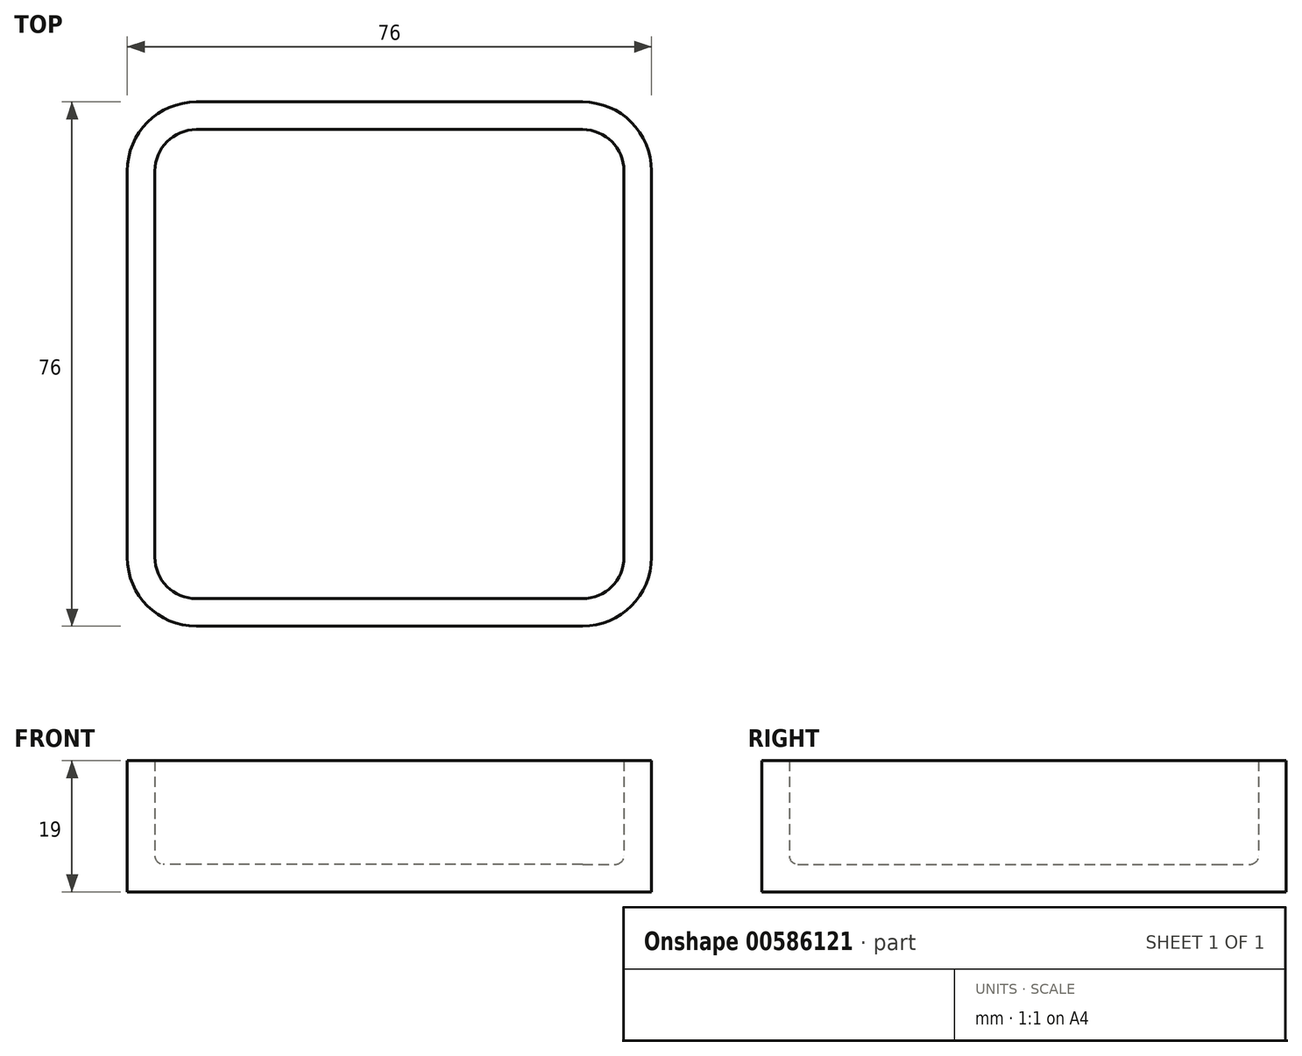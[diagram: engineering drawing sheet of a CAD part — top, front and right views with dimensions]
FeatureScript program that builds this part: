
annotation { "Feature Type Name" : "Feature", "Feature Type Description" : "" }
export const myFeature = defineFeature(function(context is Context, id is Id, definition is map)
    precondition{}
    {
        {
            var Q0;
            Q0=qCreatedBy(makeId("Top.planeOp"),FACE);
            var sketch = newSketch(context, id + "F0", { "sketchPlane" : qUnion([Q0])});
            skLineSegment(sketch, "E0.bottom", {"start": v(-34, 34) * mm, "end": v(34, 34) * mm});
            skLineSegment(sketch, "E0.top", {"start": v(-34, -34) * mm, "end": v(34, -34) * mm});
            skLineSegment(sketch, "E0.left", {"start": v(-34, 34) * mm, "end": v(-34, -34) * mm});
            skLineSegment(sketch, "E0.right", {"start": v(34, 34) * mm, "end": v(34, -34) * mm});
            skLineSegment(sketch, "E1.bottom", {"start": v(-38, 38) * mm, "end": v(38, 38) * mm});
            skLineSegment(sketch, "E1.top", {"start": v(-38, -38) * mm, "end": v(38, -38) * mm});
            skLineSegment(sketch, "E1.left", {"start": v(-38, 38) * mm, "end": v(-38, -38) * mm});
            skLineSegment(sketch, "E1.right", {"start": v(38, 38) * mm, "end": v(38, -38) * mm});
            skSolve(sketch);
        }
        {
            var Q0;
            Q0=makeQuery(id+"F0.imprint","IMPRINT",FACE,{"disambiguationData":[TD([[makeQuery(id+"F0.imprint","IMPRINT",EDGE,{"derivedFrom":sQuery(id+"F0.wireOp",EDGE,"E0.bottom")}),1.0]])]});
            var Q1;
            Q1=makeQuery(id+"F0.imprint","IMPRINT",FACE,{"disambiguationData":[TD([[makeQuery(id+"F0.imprint","IMPRINT",EDGE,{"derivedFrom":sQuery(id+"F0.wireOp",EDGE,"E0.bottom")}),-1.0]])]});
            extrude(context, id + "F1", {"entities" : qUnion([Q0, Q1]), "depth" : 4 * mm, "offsetDistance" : 25 * mm});
        }
        {
            var Q0;
            Q0=makeQuery(id+"F0.imprint","IMPRINT",FACE,{"disambiguationData":[TD([[makeQuery(id+"F0.imprint","IMPRINT",EDGE,{"derivedFrom":sQuery(id+"F0.wireOp",EDGE,"E0.bottom")}),1.0]])]});
            extrude(context, id + "F2", {"entities" : qUnion([Q0]), "operationType" : NewBodyOperationType.ADD, "depth" : 19 * mm, "offsetDistance" : 25 * mm});
        }
        {
            var Q0;
            Q0=makeQuery(id+"F2.opExtrude","SWEPT_EDGE",EDGE,{"disambiguationData":[OSD([sQuery(id+"F0.wireOp",EDGE,"E0.bottom"),sQuery(id+"F0.wireOp",EDGE,"E0.right")])]});
            var Q1;
            Q1=makeQuery(id+"F2.opExtrude","SWEPT_EDGE",EDGE,{"disambiguationData":[OSD([sQuery(id+"F0.wireOp",EDGE,"E0.top"),sQuery(id+"F0.wireOp",EDGE,"E0.right")])]});
            var Q2;
            Q2=makeQuery(id+"F2.opExtrude","SWEPT_EDGE",EDGE,{"disambiguationData":[OSD([sQuery(id+"F0.wireOp",EDGE,"E0.top"),sQuery(id+"F0.wireOp",EDGE,"E0.left")])]});
            var Q3;
            Q3=makeQuery(id+"F2.opExtrude","SWEPT_EDGE",EDGE,{"disambiguationData":[OSD([sQuery(id+"F0.wireOp",EDGE,"E0.bottom"),sQuery(id+"F0.wireOp",EDGE,"E0.left")])]});
            fillet(context, id + "F3", {"entities" : qUnion([Q0, Q1, Q2, Q3]), "radius" : 6 * mm, "tangentPropagation" : true, "allowEdgeOverflow" : false});
        }
        {
            var Q0;
            {var subQ0=sQuery(id+"F0.wireOp",EDGE,"E1.left");var subQ1=sQuery(id+"F0.wireOp",EDGE,"E1.top");Q0=makeQuery(id+"F2.boolean.opBoolean","MERGE",EDGE,{"derivedFrom":[makeQuery(id+"F1.opExtrude","SWEPT_EDGE",EDGE,{"disambiguationData":[OSD([subQ1,subQ0])]}),makeQuery(id+"F2.opExtrude","SWEPT_EDGE",EDGE,{"disambiguationData":[OSD([subQ1,subQ0])]})]});}
            var Q1;
            {var subQ0=sQuery(id+"F0.wireOp",EDGE,"E1.right");var subQ1=sQuery(id+"F0.wireOp",EDGE,"E1.top");Q1=makeQuery(id+"F2.boolean.opBoolean","MERGE",EDGE,{"derivedFrom":[makeQuery(id+"F1.opExtrude","SWEPT_EDGE",EDGE,{"disambiguationData":[OSD([subQ1,subQ0])]}),makeQuery(id+"F2.opExtrude","SWEPT_EDGE",EDGE,{"disambiguationData":[OSD([subQ1,subQ0])]})]});}
            var Q2;
            {var subQ0=sQuery(id+"F0.wireOp",EDGE,"E1.right");var subQ1=sQuery(id+"F0.wireOp",EDGE,"E1.bottom");Q2=makeQuery(id+"F2.boolean.opBoolean","MERGE",EDGE,{"derivedFrom":[makeQuery(id+"F1.opExtrude","SWEPT_EDGE",EDGE,{"disambiguationData":[OSD([subQ1,subQ0])]}),makeQuery(id+"F2.opExtrude","SWEPT_EDGE",EDGE,{"disambiguationData":[OSD([subQ1,subQ0])]})]});}
            var Q3;
            {var subQ0=sQuery(id+"F0.wireOp",EDGE,"E1.left");var subQ1=sQuery(id+"F0.wireOp",EDGE,"E1.bottom");Q3=makeQuery(id+"F2.boolean.opBoolean","MERGE",EDGE,{"derivedFrom":[makeQuery(id+"F1.opExtrude","SWEPT_EDGE",EDGE,{"disambiguationData":[OSD([subQ1,subQ0])]}),makeQuery(id+"F2.opExtrude","SWEPT_EDGE",EDGE,{"disambiguationData":[OSD([subQ1,subQ0])]})]});}
            fillet(context, id + "F4", {"entities" : qUnion([Q0, Q1, Q2, Q3]), "radius" : 10 * mm, "tangentPropagation" : true, "allowEdgeOverflow" : false});
        }
        {
            var Q0;
            Q0=makeQuery(id+"F2.boolean.opBoolean","INTERSECT",EDGE,{"derivedFrom":[makeQuery(id+"F1.opExtrude","CAP_FACE",FACE,{"disambiguationData":[OSD([sQuery(id+"F0.wireOp",EDGE,"E1.bottom"),sQuery(id+"F0.wireOp",EDGE,"E1.top"),sQuery(id+"F0.wireOp",EDGE,"E1.left"),sQuery(id+"F0.wireOp",EDGE,"E1.right")])],"isStart":false}),makeQuery(id+"F2.opExtrude","SWEPT_FACE",FACE,{"disambiguationData":[OSD([sQuery(id+"F0.wireOp",EDGE,"E0.right")])]})]});
            fillet(context, id + "F5", {"entities" : qUnion([Q0]), "radius" : 1.2 * mm, "tangentPropagation" : true, "allowEdgeOverflow" : false});
        }
    });
